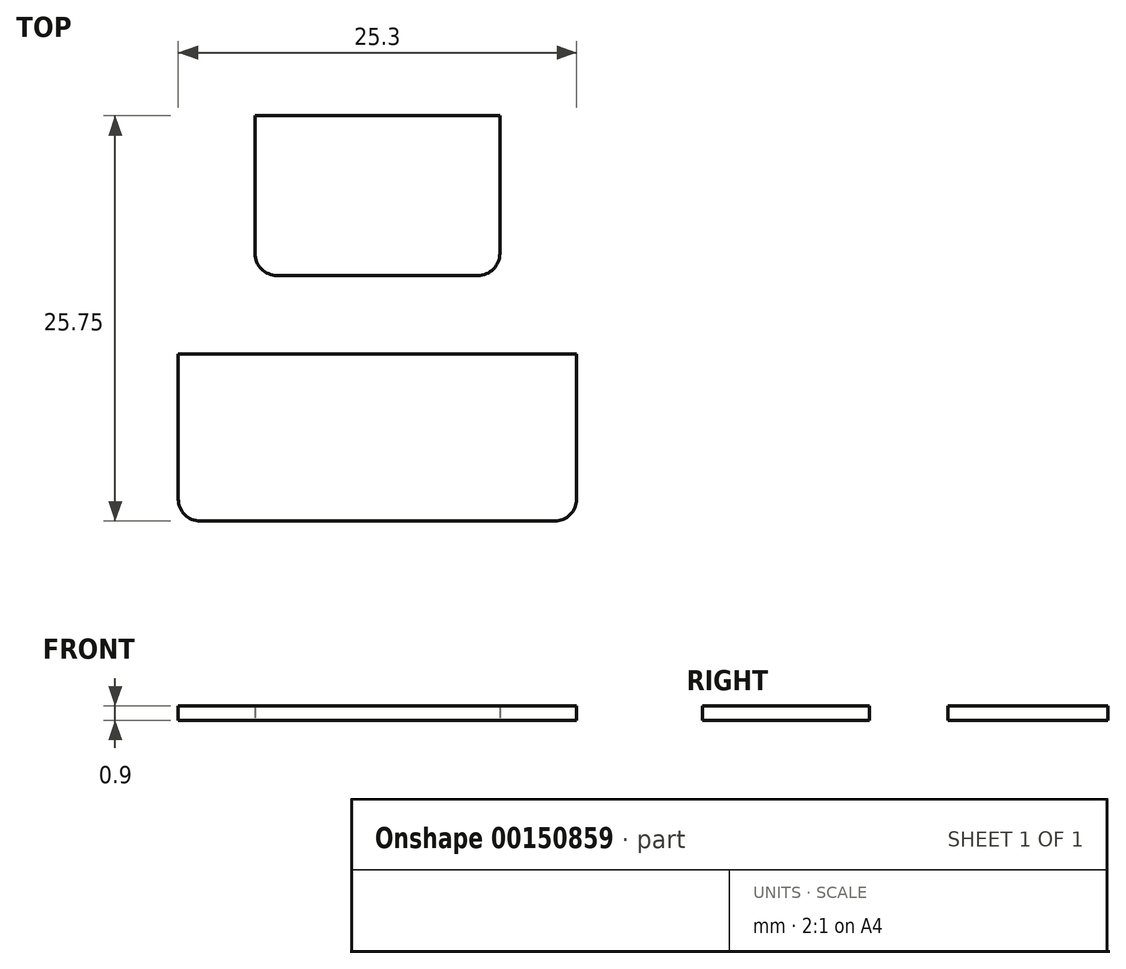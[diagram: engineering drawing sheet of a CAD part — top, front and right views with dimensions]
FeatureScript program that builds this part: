
annotation { "Feature Type Name" : "Feature", "Feature Type Description" : "" }
export const myFeature = defineFeature(function(context is Context, id is Id, definition is map)
    precondition{}
    {
        {
            var Q0;
            Q0=qCreatedBy(makeId("Top.planeOp"),FACE);
            var sketch = newSketch(context, id + "F0", { "sketchPlane" : qUnion([Q0])});
            skLineSegment(sketch, "E0.bottom", {"start": v(-12.65, 5.3) * mm, "end": v(12.65, 5.3) * mm});
            skLineSegment(sketch, "E0.top", {"start": v(-12.65, -5.3) * mm, "end": v(12.65, -5.3) * mm});
            skLineSegment(sketch, "E0.left", {"start": v(-12.65, 5.3) * mm, "end": v(-12.65, -5.3) * mm});
            skLineSegment(sketch, "E0.right", {"start": v(12.65, 5.3) * mm, "end": v(12.65, -5.3) * mm});
            skPoint(sketch, "E0.middle", {"position": v(0, 0) * mm});
            skLineSegment(sketch, "E1.bottom", {"start": v(-7.78, 20.45) * mm, "end": v(7.78, 20.45) * mm});
            skLineSegment(sketch, "E1.top", {"start": v(-7.78, 10.3) * mm, "end": v(7.77, 10.3) * mm});
            skLineSegment(sketch, "E1.left", {"start": v(-7.78, 20.45) * mm, "end": v(-7.78, 10.3) * mm});
            skLineSegment(sketch, "E1.right", {"start": v(7.78, 20.45) * mm, "end": v(7.77, 10.3) * mm});
            skPoint(sketch, "E1.middle", {"position": v(0, 15.38) * mm});
            skSolve(sketch);
        }
        {
            var Q0;
            Q0=makeQuery(id+"F0.imprint","IMPRINT",FACE,{"disambiguationData":[TD([[makeQuery(id+"F0.imprint","IMPRINT",EDGE,{"derivedFrom":sQuery(id+"F0.wireOp",EDGE,"E0.bottom")}),-1.0]])]});
            var Q1;
            Q1=makeQuery(id+"F0.imprint","IMPRINT",FACE,{"disambiguationData":[TD([[makeQuery(id+"F0.imprint","IMPRINT",EDGE,{"derivedFrom":sQuery(id+"F0.wireOp",EDGE,"E1.bottom")}),-1.0]])]});
            extrude(context, id + "F1", {"entities" : qUnion([Q0, Q1]), "depth" : .90 * mm});
        }
        {
            var Q0;
            Q0=makeQuery(id+"F1.opExtrude","SWEPT_EDGE",EDGE,{"disambiguationData":[OSD([sQuery(id+"F0.wireOp",EDGE,"E0.top"),sQuery(id+"F0.wireOp",EDGE,"E0.left")])]});
            var Q1;
            Q1=makeQuery(id+"F1.opExtrude","SWEPT_EDGE",EDGE,{"disambiguationData":[OSD([sQuery(id+"F0.wireOp",EDGE,"E0.top"),sQuery(id+"F0.wireOp",EDGE,"E0.right")])]});
            var Q2;
            Q2=makeQuery(id+"F1.opExtrude","SWEPT_EDGE",EDGE,{"disambiguationData":[OSD([sQuery(id+"F0.wireOp",EDGE,"E1.top"),sQuery(id+"F0.wireOp",EDGE,"E1.right")])]});
            var Q3;
            Q3=makeQuery(id+"F1.opExtrude","SWEPT_EDGE",EDGE,{"disambiguationData":[OSD([sQuery(id+"F0.wireOp",EDGE,"E1.top"),sQuery(id+"F0.wireOp",EDGE,"E1.left")])]});
            fillet(context, id + "F2", {"entities" : qUnion([Q0, Q1, Q2, Q3]), "radius" : 1.4 * mm, "tangentPropagation" : true, "allowEdgeOverflow" : false});
        }
    });
